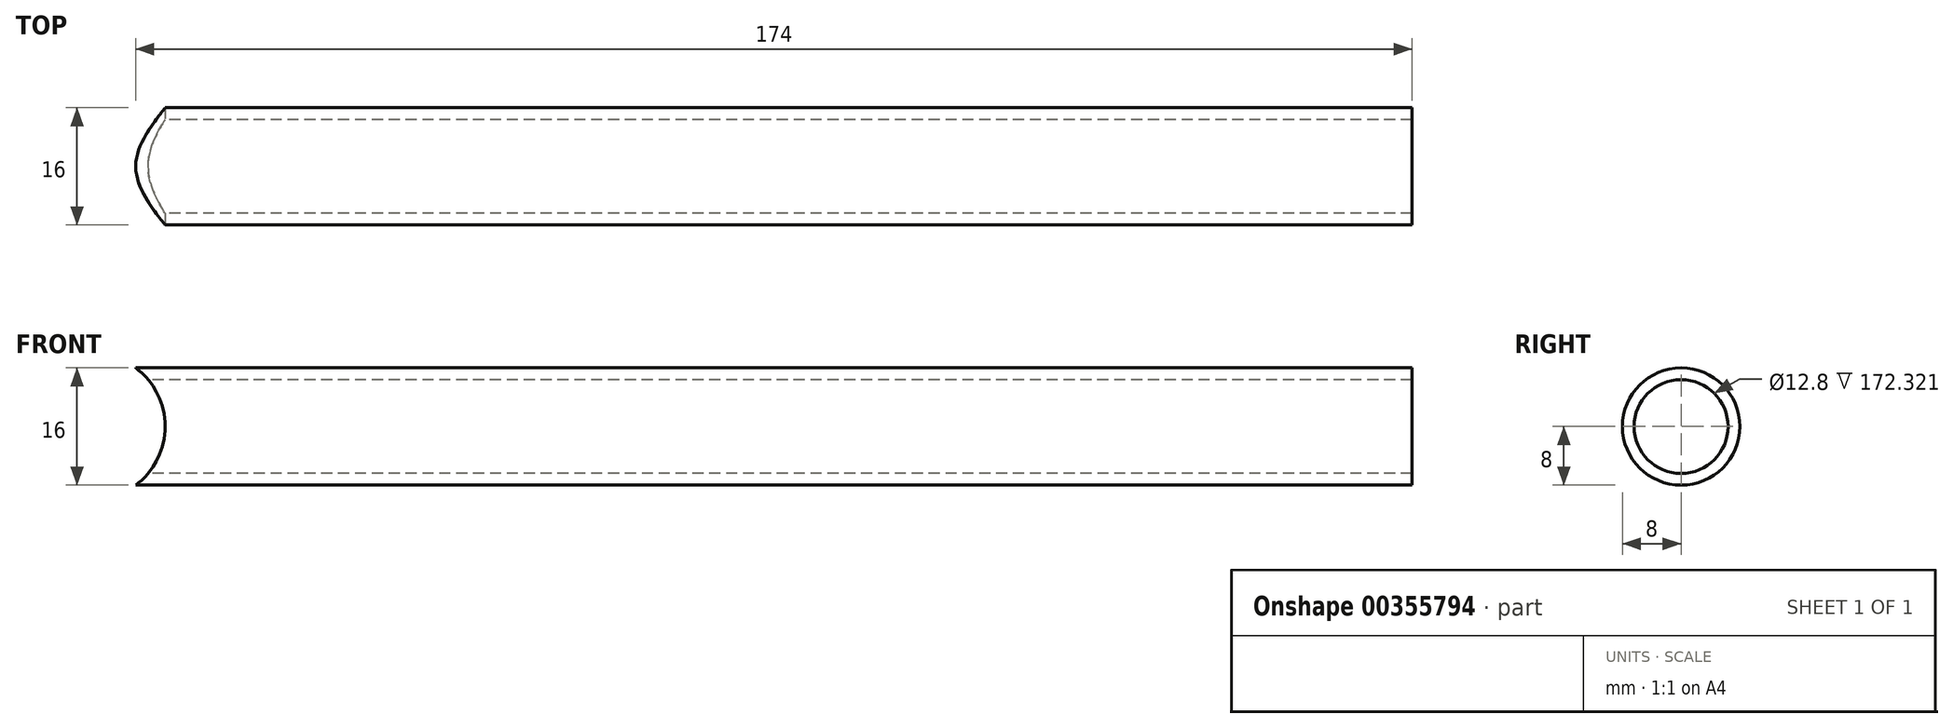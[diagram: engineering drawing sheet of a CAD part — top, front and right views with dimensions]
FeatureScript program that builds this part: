
annotation { "Feature Type Name" : "Feature", "Feature Type Description" : "" }
export const myFeature = defineFeature(function(context is Context, id is Id, definition is map)
    precondition{}
    {
        {
            var Q0;
            Q0=qCreatedBy(makeId("Right.planeOp"),FACE);
            var sketch = newSketch(context, id + "F0", { "sketchPlane" : qUnion([Q0])});
            skCircle(sketch, "E0", {"center": v(0, 0) * mm, "radius": 8 * mm});
            skCircle(sketch, "E1", {"center": v(0, 0) * mm, "radius": 6.4 * mm});
            skSolve(sketch);
        }
        {
            var Q0;
            Q0=qSketchRegion(id+"F0",true);
            extrude(context, id + "F1", {"entities" : qUnion([Q0]), "depth" : 180 * mm});
        }
        {
            var Q0;
            Q0=qCreatedBy(makeId("Front.planeOp"),FACE);
            var sketch = newSketch(context, id + "F2", { "sketchPlane" : qUnion([Q0])});
            skCircle(sketch, "E2", {"center": v(0, 0) * mm, "radius": 10 * mm});
            skSolve(sketch);
        }
        {
            var Q0;
            Q0=qSketchRegion(id+"F2",true);
            extrude(context, id + "F3", {"entities" : qUnion([Q0]), "operationType" : NewBodyOperationType.REMOVE, "oppositeDirection" : true, "depth" : 25 * mm, "hasSecondDirection" : true, "secondDirectionOppositeDirection" : false, "secondDirectionDepth" : 25 * mm});
        }
    });
